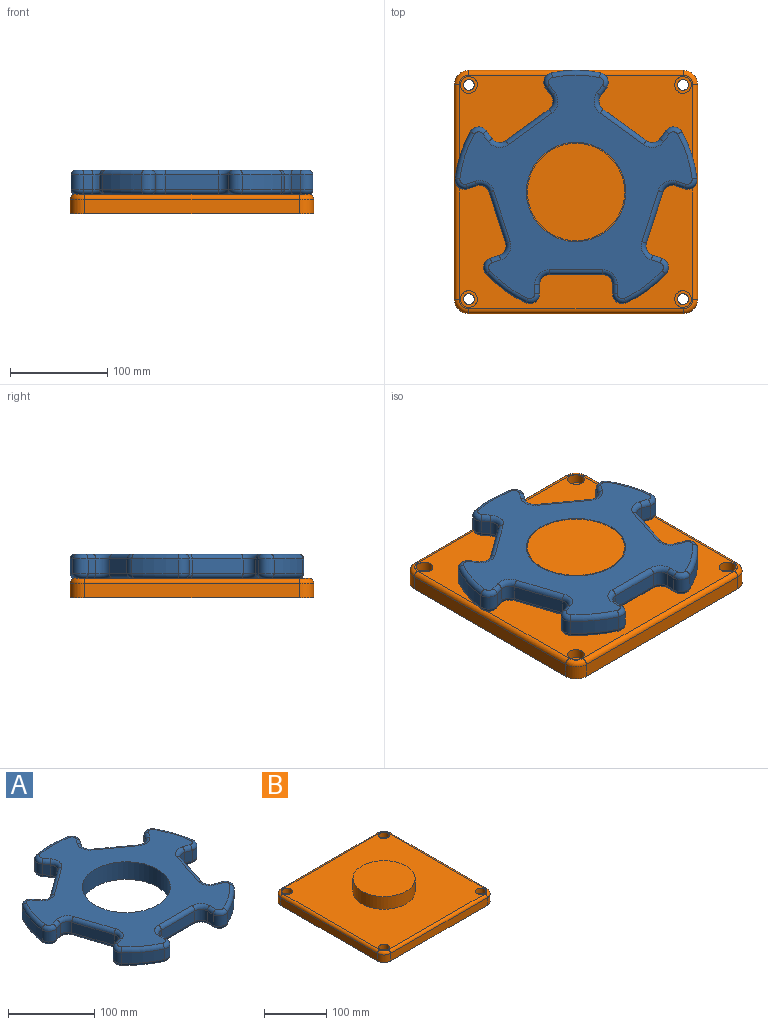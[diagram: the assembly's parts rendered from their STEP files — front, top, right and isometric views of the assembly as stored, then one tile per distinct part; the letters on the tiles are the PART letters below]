
ASSEMBLY  parts=2 mates=1
PART A: 123 faces, bbox 268.9x258.5x25 mm
  f0: plane 238.57x229.73mm, normal (0,0,1), area 21505.7mm2, adj f6,f83,f84,f85,f86,f87,f88,f89
  f1: plane 238.57x229.73mm, normal (0,0,-1), area 21505.7mm2, adj f6,f43,f44,f45,f46,f47,f48,f49
  f2: cylinder r=125mm len=47.82mm, axis (0,0,-1), area 759.5mm2, adj f34,f42,f74,f114
  f3: cylinder r=125mm len=50.29mm, axis (0,0,-1), area 759.5mm2, adj f27,f35,f75,f115
  f4: cylinder r=125mm len=47.82mm, axis (0,0,-1), area 759.5mm2, adj f20,f28,f59,f99
  f5: cylinder r=125mm len=40.68mm, axis (0,0,-1), area 759.5mm2, adj f13,f21,f43,f83
  f6: cylinder r=51mm len=102mm, axis (0,0,-1), area 8011.1mm2, adj f0,f1
  f7: cylinder r=125mm len=40.68mm, axis (0,0,-1), area 759.5mm2, adj f14,f41,f58,f98
  f8: plane 15x9.73mm, normal (-1,0,0), area 146mm2, adj f11,f14,f54,f94
  f9: plane 55x15mm, normal (0,-1,0), area 825mm2, adj f11,f12,f50,f90
  f10: plane 15x9.73mm, normal (1,0,0), area 146mm2, adj f12,f13,f46,f86
  f11: cylinder r=10mm len=15mm, axis (0,0,-1), area 235.6mm2, adj f8,f9,f52,f92
  f12: cylinder r=10mm len=15mm, axis (0,0,-1), area 235.6mm2, adj f9,f10,f48,f88
  f13: cylinder r=10mm len=15mm, axis (0,0,-1), area 299.5mm2, adj f5,f10,f44,f84
  f14: cylinder r=10mm len=15mm, axis (0,0,-1), area 299.5mm2, adj f7,f8,f56,f96
  f15: plane 15x9.26mm, normal (-0.31,0.95,0), area 146mm2, adj f18,f21,f47,f87
  f16: plane 52.31x17mm, normal (-0.95,-0.31,0), area 825mm2, adj f18,f19,f51,f91
  f17: plane 15x9.26mm, normal (0.31,-0.95,0), area 146mm2, adj f19,f20,f55,f95
  f18: cylinder r=10mm len=15mm, axis (0,0,-1), area 235.6mm2, adj f15,f16,f49,f89
  f19: cylinder r=10mm len=15mm, axis (0,0,-1), area 235.6mm2, adj f16,f17,f53,f93
  f20: cylinder r=10mm len=15mm, axis (0,0,-1), area 299.5mm2, adj f4,f17,f57,f97
  f21: cylinder r=10mm len=16.25mm, axis (0,0,-1), area 299.5mm2, adj f5,f15,f45,f85
  f22: plane 15x7.87mm, normal (0.81,0.59,0), area 146mm2, adj f25,f28,f63,f103
  f23: plane 44.5x32.33mm, normal (-0.59,0.81,0), area 825mm2, adj f25,f26,f67,f107
  f24: plane 15x7.87mm, normal (-0.81,-0.59,0), area 146mm2, adj f26,f27,f71,f111
  f25: cylinder r=10mm len=15mm, axis (0,0,-1), area 235.6mm2, adj f22,f23,f65,f105
  f26: cylinder r=10mm len=15mm, axis (0,0,-1), area 235.6mm2, adj f23,f24,f69,f109
  f27: cylinder r=10mm len=15.67mm, axis (0,0,-1), area 299.5mm2, adj f3,f24,f73,f113
  f28: cylinder r=10mm len=16.78mm, axis (0,0,-1), area 299.5mm2, adj f4,f22,f61,f101
  f29: plane 15x7.87mm, normal (0.81,-0.59,0), area 146mm2, adj f32,f35,f79,f119
  f30: plane 44.5x32.33mm, normal (0.59,0.81,0), area 825mm2, adj f32,f33,f82,f122
  f31: plane 15x7.87mm, normal (-0.81,0.59,0), area 146mm2, adj f33,f34,f78,f118
  f32: cylinder r=10mm len=15mm, axis (0,0,-1), area 235.6mm2, adj f29,f30,f81,f121
  f33: cylinder r=10mm len=15mm, axis (0,0,-1), area 235.6mm2, adj f30,f31,f80,f120
  f34: cylinder r=10mm len=16.78mm, axis (0,0,-1), area 299.5mm2, adj f2,f31,f76,f116
  f35: cylinder r=10mm len=15.67mm, axis (0,0,-1), area 299.5mm2, adj f3,f29,f77,f117
  f36: plane 15x9.26mm, normal (-0.31,-0.95,0), area 146mm2, adj f39,f42,f70,f110
  f37: plane 52.31x17mm, normal (0.95,-0.31,0), area 825mm2, adj f39,f40,f66,f106
  f38: plane 15x9.26mm, normal (0.31,0.95,0), area 146mm2, adj f40,f41,f62,f102
  f39: cylinder r=10mm len=15mm, axis (0,0,-1), area 235.6mm2, adj f36,f37,f68,f108
  f40: cylinder r=10mm len=15mm, axis (0,0,-1), area 235.6mm2, adj f37,f38,f64,f104
  f41: cylinder r=10mm len=16.25mm, axis (0,0,-1), area 299.5mm2, adj f7,f38,f60,f100
  f42: cylinder r=10mm len=15mm, axis (0,0,-1), area 299.5mm2, adj f2,f36,f72,f112
  f43: torus R=120mm, axis (0,0,1), area 391.9mm2, adj f1,f5,f44,f45
  f44: torus R=5mm, axis (0,0,1), area 128.3mm2, adj f1,f13,f43,f46
  f45: torus R=5mm, axis (0,0,1), area 128.3mm2, adj f1,f21,f43,f47
  f46: cylinder r=5mm len=9.73mm, axis (0,-1,0), area 76.4mm2, adj f1,f10,f44,f48
  f47: cylinder r=5mm len=10.8mm, axis (0.95,0.31,0), area 76.4mm2, adj f1,f15,f45,f49
  f48: torus R=15mm, axis (0,0,1), area 145.8mm2, adj f1,f12,f46,f50
  f49: torus R=15mm, axis (0,0,1), area 145.8mm2, adj f1,f18,f47,f51
  f50: cylinder r=5mm len=55mm, axis (-1,0,0), area 432mm2, adj f1,f9,f48,f52
  f51: cylinder r=5mm len=53.85mm, axis (-0.31,0.95,0), area 432mm2, adj f1,f16,f49,f53
  f52: torus R=15mm, axis (0,0,1), area 145.8mm2, adj f1,f11,f50,f54
  f53: torus R=15mm, axis (0,0,1), area 145.8mm2, adj f1,f19,f51,f55
  f54: cylinder r=5mm len=9.73mm, axis (0,1,0), area 76.4mm2, adj f1,f8,f52,f56
  f55: cylinder r=5mm len=10.8mm, axis (-0.95,-0.31,0), area 76.4mm2, adj f1,f17,f53,f57
  f56: torus R=5mm, axis (0,0,1), area 128.3mm2, adj f1,f14,f54,f58
  f57: torus R=5mm, axis (0,0,1), area 128.3mm2, adj f1,f20,f55,f59
  f58: torus R=120mm, axis (0,0,1), area 391.9mm2, adj f1,f7,f56,f60
  f59: torus R=120mm, axis (0,0,1), area 391.9mm2, adj f1,f4,f57,f61
  f60: torus R=5mm, axis (0,0,1), area 128.3mm2, adj f1,f41,f58,f62
  f61: torus R=5mm, axis (0,0,1), area 128.3mm2, adj f1,f28,f59,f63
  f62: cylinder r=5mm len=10.8mm, axis (0.95,-0.31,0), area 76.4mm2, adj f1,f38,f60,f64
  f63: cylinder r=5mm len=10.81mm, axis (0.59,-0.81,0), area 76.4mm2, adj f1,f22,f61,f65
  f64: torus R=15mm, axis (0,0,1), area 145.8mm2, adj f1,f40,f62,f66
  f65: torus R=15mm, axis (0,0,1), area 145.8mm2, adj f1,f25,f63,f67
  f66: cylinder r=5mm len=53.85mm, axis (-0.31,-0.95,0), area 432mm2, adj f1,f37,f64,f68
  f67: cylinder r=5mm len=47.44mm, axis (0.81,0.59,0), area 432mm2, adj f1,f23,f65,f69
  f68: torus R=15mm, axis (0,0,1), area 145.8mm2, adj f1,f39,f66,f70
  f69: torus R=15mm, axis (0,0,1), area 145.8mm2, adj f1,f26,f67,f71
  f70: cylinder r=5mm len=10.8mm, axis (-0.95,0.31,0), area 76.4mm2, adj f1,f36,f68,f72
  f71: cylinder r=5mm len=10.81mm, axis (-0.59,0.81,0), area 76.4mm2, adj f1,f24,f69,f73
  f72: torus R=5mm, axis (0,0,1), area 128.3mm2, adj f1,f42,f70,f74
  f73: torus R=5mm, axis (0,0,1), area 128.3mm2, adj f1,f27,f71,f75
  f74: torus R=120mm, axis (0,0,1), area 391.9mm2, adj f1,f2,f72,f76
  f75: torus R=120mm, axis (0,0,1), area 391.9mm2, adj f1,f3,f73,f77
  f76: torus R=5mm, axis (0,0,1), area 128.3mm2, adj f1,f34,f74,f78
  f77: torus R=5mm, axis (0,0,1), area 128.3mm2, adj f1,f35,f75,f79
  f78: cylinder r=5mm len=10.81mm, axis (0.59,0.81,0), area 76.4mm2, adj f1,f31,f76,f80
  f79: cylinder r=5mm len=10.81mm, axis (-0.59,-0.81,0), area 76.4mm2, adj f1,f29,f77,f81
  f80: torus R=15mm, axis (0,0,1), area 145.8mm2, adj f1,f33,f78,f82
  f81: torus R=15mm, axis (0,0,1), area 145.8mm2, adj f1,f32,f79,f82
  f82: cylinder r=5mm len=47.44mm, axis (0.81,-0.59,0), area 432mm2, adj f1,f30,f80,f81
  f83: torus R=120mm, axis (0,0,1), area 391.9mm2, adj f0,f5,f84,f85
  f84: torus R=5mm, axis (0,0,1), area 128.3mm2, adj f0,f13,f83,f86
  f85: torus R=5mm, axis (0,0,1), area 128.3mm2, adj f0,f21,f83,f87
  f86: cylinder r=5mm len=9.73mm, axis (0,1,0), area 76.4mm2, adj f0,f10,f84,f88
  f87: cylinder r=5mm len=10.8mm, axis (-0.95,-0.31,0), area 76.4mm2, adj f0,f15,f85,f89
  f88: torus R=15mm, axis (0,0,1), area 145.8mm2, adj f0,f12,f86,f90
  f89: torus R=15mm, axis (0,0,1), area 145.8mm2, adj f0,f18,f87,f91
  f90: cylinder r=5mm len=55mm, axis (1,0,0), area 432mm2, adj f0,f9,f88,f92
  f91: cylinder r=5mm len=53.85mm, axis (0.31,-0.95,0), area 432mm2, adj f0,f16,f89,f93
  f92: torus R=15mm, axis (0,0,1), area 145.8mm2, adj f0,f11,f90,f94
  f93: torus R=15mm, axis (0,0,1), area 145.8mm2, adj f0,f19,f91,f95
  f94: cylinder r=5mm len=9.73mm, axis (0,-1,0), area 76.4mm2, adj f0,f8,f92,f96
  f95: cylinder r=5mm len=10.8mm, axis (0.95,0.31,0), area 76.4mm2, adj f0,f17,f93,f97
  f96: torus R=5mm, axis (0,0,1), area 128.3mm2, adj f0,f14,f94,f98
  f97: torus R=5mm, axis (0,0,1), area 128.3mm2, adj f0,f20,f95,f99
  f98: torus R=120mm, axis (0,0,1), area 391.9mm2, adj f0,f7,f96,f100
  f99: torus R=120mm, axis (0,0,1), area 391.9mm2, adj f0,f4,f97,f101
  f100: torus R=5mm, axis (0,0,1), area 128.3mm2, adj f0,f41,f98,f102
  f101: torus R=5mm, axis (0,0,1), area 128.3mm2, adj f0,f28,f99,f103
  f102: cylinder r=5mm len=10.8mm, axis (-0.95,0.31,0), area 76.4mm2, adj f0,f38,f100,f104
  f103: cylinder r=5mm len=10.81mm, axis (-0.59,0.81,0), area 76.4mm2, adj f0,f22,f101,f105
  f104: torus R=15mm, axis (0,0,1), area 145.8mm2, adj f0,f40,f102,f106
  f105: torus R=15mm, axis (0,0,1), area 145.8mm2, adj f0,f25,f103,f107
  f106: cylinder r=5mm len=53.85mm, axis (0.31,0.95,0), area 432mm2, adj f0,f37,f104,f108
  f107: cylinder r=5mm len=47.44mm, axis (-0.81,-0.59,0), area 432mm2, adj f0,f23,f105,f109
  f108: torus R=15mm, axis (0,0,1), area 145.8mm2, adj f0,f39,f106,f110
  f109: torus R=15mm, axis (0,0,1), area 145.8mm2, adj f0,f26,f107,f111
  f110: cylinder r=5mm len=10.8mm, axis (0.95,-0.31,0), area 76.4mm2, adj f0,f36,f108,f112
  f111: cylinder r=5mm len=10.81mm, axis (0.59,-0.81,0), area 76.4mm2, adj f0,f24,f109,f113
  f112: torus R=5mm, axis (0,0,1), area 128.3mm2, adj f0,f42,f110,f114
  f113: torus R=5mm, axis (0,0,1), area 128.3mm2, adj f0,f27,f111,f115
  f114: torus R=120mm, axis (0,0,1), area 391.9mm2, adj f0,f2,f112,f116
  f115: torus R=120mm, axis (0,0,1), area 391.9mm2, adj f0,f3,f113,f117
  f116: torus R=5mm, axis (0,0,1), area 128.3mm2, adj f0,f34,f114,f118
  f117: torus R=5mm, axis (0,0,1), area 128.3mm2, adj f0,f35,f115,f119
  f118: cylinder r=5mm len=10.81mm, axis (-0.59,-0.81,0), area 76.4mm2, adj f0,f31,f116,f120
  f119: cylinder r=5mm len=10.81mm, axis (0.59,0.81,0), area 76.4mm2, adj f0,f29,f117,f121
  f120: torus R=15mm, axis (0,0,1), area 145.8mm2, adj f0,f33,f118,f122
  f121: torus R=15mm, axis (0,0,1), area 145.8mm2, adj f0,f32,f119,f122
  f122: cylinder r=5mm len=47.44mm, axis (-0.81,0.59,0), area 432mm2, adj f0,f30,f120,f121
PART B: 32 faces, bbox 252.5x252.5x45 mm
  f0: plane 220x15mm, normal (1,0,0), area 3300mm2, adj f5,f8,f11,f27
  f1: plane 220x15mm, normal (0,1,0), area 3300mm2, adj f5,f8,f9,f31
  f2: plane 220x15mm, normal (-1,0,0), area 3300mm2, adj f5,f9,f10,f28
  f3: plane 220x15mm, normal (0,-1,0), area 3300mm2, adj f5,f10,f11,f24
  f4: plane 240x240mm, normal (0,0,1), area 48725.4mm2, adj f6,f14,f17,f20,f23,f24,f25,f26
  f5: plane 250x250mm, normal (0,0,-1), area 61926.7mm2, adj f0,f1,f2,f3,f8,f9,f10,f11
  f6: cylinder r=50mm len=100mm, axis (0,0,-1), area 7854mm2, adj f4,f7
  f7: plane 100x100mm, normal (0,0,1), area 7854mm2, adj f6
  f8: cylinder r=15mm len=15mm, axis (0,0,-1), area 353.4mm2, adj f0,f1,f5,f29
  f9: cylinder r=15mm len=15mm, axis (0,0,1), area 353.4mm2, adj f1,f2,f5,f30
  f10: cylinder r=15mm len=15mm, axis (0,0,-1), area 353.4mm2, adj f2,f3,f5,f26
  f11: cylinder r=15mm len=15mm, axis (0,0,1), area 353.4mm2, adj f0,f3,f5,f25
  f12: cylinder r=5.5mm len=11mm, axis (0,0,1), area 345.6mm2, adj f5,f13
  f13: plane 17.25x17.25mm, normal (0,0,1), area 138.7mm2, adj f12,f14
  f14: cylinder r=8.62mm len=17.25mm, axis (0,0,1), area 541.9mm2, adj f4,f13
  f15: cylinder r=5.5mm len=11mm, axis (0,0,1), area 345.6mm2, adj f5,f16
  f16: plane 17.25x17.25mm, normal (0,0,1), area 138.7mm2, adj f15,f17
  f17: cylinder r=8.62mm len=17.25mm, axis (0,0,1), area 541.9mm2, adj f4,f16
  f18: cylinder r=5.5mm len=11mm, axis (0,0,1), area 345.6mm2, adj f5,f19
  f19: plane 17.25x17.25mm, normal (0,0,1), area 138.7mm2, adj f18,f20
  f20: cylinder r=8.62mm len=17.25mm, axis (0,0,1), area 541.9mm2, adj f4,f19
  f21: cylinder r=5.5mm len=11mm, axis (0,0,1), area 345.6mm2, adj f5,f22
  f22: plane 17.25x17.25mm, normal (0,0,1), area 138.7mm2, adj f21,f23
  f23: cylinder r=8.62mm len=17.25mm, axis (0,0,1), area 541.9mm2, adj f4,f22
  f24: cylinder r=5mm len=220mm, axis (-1,0,0), area 1727.9mm2, adj f3,f4,f25,f26
  f25: torus R=10mm, axis (0,0,1), area 162.6mm2, adj f4,f11,f24,f27
  f26: torus R=10mm, axis (0,0,1), area 162.6mm2, adj f4,f10,f24,f28
  f27: cylinder r=5mm len=220mm, axis (0,-1,0), area 1727.9mm2, adj f0,f4,f25,f29
  f28: cylinder r=5mm len=220mm, axis (0,1,0), area 1727.9mm2, adj f2,f4,f26,f30
  f29: torus R=10mm, axis (0,0,1), area 162.6mm2, adj f4,f8,f27,f31
  f30: torus R=10mm, axis (0,0,1), area 162.6mm2, adj f4,f9,f28,f31
  f31: cylinder r=5mm len=220mm, axis (1,0,0), area 1727.9mm2, adj f1,f4,f29,f30
PLACE A at identity
PLACE B at identity fixed
MATE revolute A.f2 <-> B.f6  axis (0,0,1) through (0,0,45)mm
